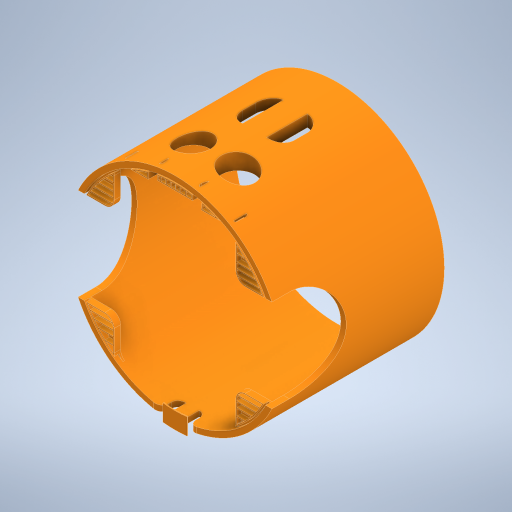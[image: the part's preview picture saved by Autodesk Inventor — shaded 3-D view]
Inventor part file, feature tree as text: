
AUTODESK INVENTOR PART (.ipt)
format: ipt  version: 2023 (Build 270158000, 158)  size: 878,592 bytes
history: native  units: mm
features: extrude x17, sketch x12, projected_geometry x12, fillet x9, plane x3, mirror x2, other x1
ambient origin geometry x8: Origin, YZ Plane, XZ Plane, XY Plane, X Axis, Y Axis, Z Axis, Center Point
bodies: Body1 (feature_tree)
feature tree (56):
  other  "Sólido1"
  sketch  "Boceto1"  dims[d0=110.0mm d1=3.0mm]
  extrude  "Extrusión1"  Depth=3.0mm
  extrude  "Extrusión2"  Depth=18.0mm
  extrude  "Extrusión3"  Depth=29.04mm
  extrude  "Extrusión4"  Depth=9.0mm
  sketch  "Boceto3"  dims[d5=4.5mm d6=29.04mm]
  extrude  "Extrusión5"  Depth=7.0mm TaperAngle=0.0deg
  fillet  "Empalme1"  Radius=60.0mm
  fillet  "Empalme2"  Radius=1.0mm
  fillet  "Empalme3"  Radius=7.0mm
  fillet  "Empalme4"  Radius=25.0mm
  fillet  "Empalme5"  Radius=53.0mm
  fillet  "Empalme6"  Radius=25.0mm
  fillet  "Empalme7"  Radius=1.0mm
  fillet  "Empalme8"  Radius=20.0mm
  sketch  "Boceto4"  dims[d7=41.91mm d8=9.0mm]
  extrude  "Extrusión6"  Depth=4.0mm
  extrude  "Extrusión7"  Depth=4.0mm
  extrude  "Extrusión8"  Depth=5.0mm
  sketch  "Boceto5"  dims[d9=15.0mm d10=2.5mm d11=0.0mm d12=60.0mm d13=1.0mm d14=0.0mm d15=7.0mm d16=0.0mm d18=25.0mm d19=0.0mm d20=53.0mm d21=0.0mm d22=25.0mm d23=1.0mm d24=20.0mm]
  extrude  "Extrusión9"  Depth=5.0mm
  fillet  "Empalme9"  Radius=21.0mm
  extrude  "Extrusión10"  Depth=2.0mm
  extrude  "Extrusión11"  Depth=18.0mm
  extrude  "Extrusión12"  Depth=3.0mm TaperAngle=0.0deg
  extrude  "Extrusión13"  Depth=3.0mm
  extrude  "Extrusión14"  Depth=3.0mm TaperAngle=0.0deg
  mirror  "Simetría1"
  mirror  "Simetría2"
  extrude  "Extrusión15"  Depth=3.0mm
  extrude  "Extrusión16"  Depth=3.0mm
  extrude  "Extrusión17"  Depth=3.0mm
  sketch  "Boceto2"  dims[d3=50.0mm d4=18.0mm]
  projected_geometry  "Contorno proyectado1"
  projected_geometry  "Contorno proyectado2"
  projected_geometry  "Contorno proyectado3"
  sketch  "Boceto6"  dims[d25=4.0mm d26=4.0mm]
  projected_geometry  "Contorno proyectado4"
  sketch  "Boceto7"  dims[d27=50.0mm d28=4.0mm]
  projected_geometry  "Contorno proyectado5"
  projected_geometry  "Contorno proyectado6"
  sketch  "Boceto8"  dims[d29=5.0mm d30=5.0mm]
  projected_geometry  "Contorno proyectado7"
  sketch  "Boceto9"  dims[d31=5.0mm d32=12.5mm d33=21.0mm]
  projected_geometry  "Contorno proyectado8"
  plane  "Plano de trabajo1"
  plane  "Plano de trabajo2"
  plane  "Plano de trabajo3"
  sketch  "Boceto10"  dims[d34=45.0mm d35=2.0mm]
  projected_geometry  "Contorno proyectado9"
  sketch  "Boceto11"  dims[d36=24.0mm d37=18.0mm]
  projected_geometry  "Contorno proyectado10"
  sketch  "Boceto12"  dims[d38=12.0mm d39=2.5mm d40=0.0mm d41=40.0mm d42=40.0mm d43=0.0mm d44=1.0mm d45=8.25mm d46=20.5mm d47=0.5mm d48=0.0mm d49=8.75mm d50=20.5mm d51=32.0mm d52=15.0mm d53=28.0mm d54=22.0mm d55=6.0mm d56=0.5mm d57=0.0mm d58=7.5mm d59=1.0mm d60=27.25mm d61=2.0mm d62=0.5mm d63=0.0mm d65=0.5mm d66=51.0mm d67=0.0mm d68=0.5mm d69=0.5mm d70=0.0mm d71=0.0mm d72=0.5mm d73=10.0mm d74=0.0mm d75=0.0mm d76=0.5mm d77=0.5mm d78=0.5mm d81=0.5mm d82=0.5mm d83=10.0mm d84=0.0mm d85=0.0mm d86=0.5mm d87=0.5mm d88=0.5mm d89=2.0mm d90=0.5mm d91=2.5mm d92=0.5mm d93=0.5mm d94=0.5mm d95=2.5mm d96=2.0mm d97=2.0mm d98=10.0mm d99=0.0mm d100=0.5mm d101=0.5mm d102=0.5mm d103=3.5mm d104=1.0mm d105=3.5mm d106=0.5mm d107=0.5mm d108=3.0mm d109=0.5mm d110=0.0mm d111=0.5mm d112=0.5mm d113=0.5mm d114=0.0mm d115=0.5mm]
  projected_geometry  "Contorno proyectado11"
  projected_geometry  "Contorno proyectado12"
